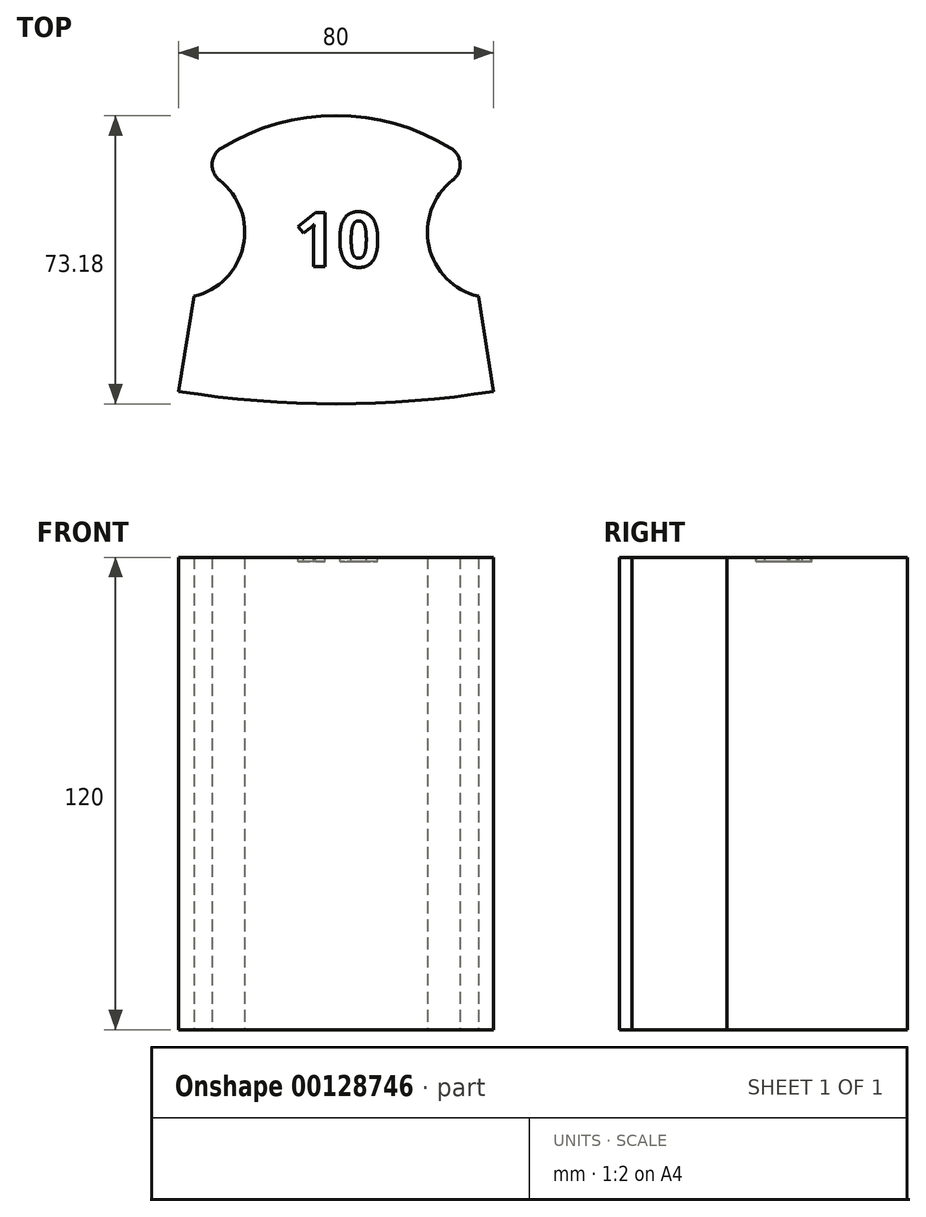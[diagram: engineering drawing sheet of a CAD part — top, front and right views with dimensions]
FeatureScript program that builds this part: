
annotation { "Feature Type Name" : "Feature", "Feature Type Description" : "" }
export const myFeature = defineFeature(function(context is Context, id is Id, definition is map)
    precondition{}
    {
        {
            var Q0;
            Q0=qCreatedBy(makeId("Top.planeOp"),FACE);
            var sketch = newSketch(context, id + "F0", { "sketchPlane" : qUnion([Q0])});
            skLineSegment(sketch, "E0", {"start": v(0, 0) * mm, "end": v(3.87, 24.16) * mm});
            skLineSegment(sketch, "E1", {"start": v(0, 0) * mm, "end": v(80, 0) * mm, "construction": true});
            skLineSegment(sketch, "E2", {"start": v(40, 0) * mm, "end": v(40, 70) * mm, "construction": true});
            skArc(sketch, "E3", {"start": v(3.87, 24.16) * mm, "mid": v(16.4, 36.85) * mm, "end": v(10.4, 53.64) * mm});
            skArc(sketch, "E4.MirrorCS", {"start": v(76.13, 24.16) * mm, "mid": v(63.6, 36.85) * mm, "end": v(69.6, 53.64) * mm});
            skLineSegment(sketch, "E5.MirrorCS", {"start": v(80, 0) * mm, "end": v(76.13, 24.16) * mm});
            skArc(sketch, "E6", {"start": v(69.1, 61.84) * mm, "mid": v(40, 70) * mm, "end": v(10.9, 61.84) * mm});
            skPoint(sketch, "E7.visualSharp", {"position": v(3.87, 56.79) * mm});
            skArc(sketch, "E7.filletArc", {"start": v(10.9, 61.84) * mm, "mid": v(8.5, 57.87) * mm, "end": v(10.4, 53.64) * mm});
            skPoint(sketch, "E8.visualSharp", {"position": v(76.13, 56.79) * mm});
            skArc(sketch, "E8.filletArc", {"start": v(69.6, 53.64) * mm, "mid": v(71.5, 57.87) * mm, "end": v(69.1, 61.84) * mm});
            skArc(sketch, "E9", {"start": v(0, 0) * mm, "mid": v(40, -3.18) * mm, "end": v(80, 0) * mm});
            skSolve(sketch);
        }
        {
            var Q0;
            Q0=makeQuery(id+"F0.imprint","IMPRINT",FACE,{"disambiguationData":[TD([[makeQuery(id+"F0.imprint","IMPRINT",EDGE,{"derivedFrom":sQuery(id+"F0.wireOp",EDGE,"E0")}),-1.0]])]});
            extrude(context, id + "F1", {"entities" : qUnion([Q0]), "depth" : 120 * mm});
        }
        {
            var Q0;
            Q0=makeQuery(id+"F1.opExtrude","CAP_FACE",FACE,{"disambiguationData":[OSD([sQuery(id+"F0.wireOp",EDGE,"E0"),sQuery(id+"F0.wireOp",EDGE,"E3"),sQuery(id+"F0.wireOp",EDGE,"E4.MirrorCS"),sQuery(id+"F0.wireOp",EDGE,"E5.MirrorCS"),sQuery(id+"F0.wireOp",EDGE,"E6"),sQuery(id+"F0.wireOp",EDGE,"E7.filletArc"),sQuery(id+"F0.wireOp",EDGE,"E8.filletArc"),sQuery(id+"F0.wireOp",EDGE,"E9")])],"isStart":false});
            var sketch = newSketch(context, id + "F2", { "sketchPlane" : qUnion([Q0])});
            skText(sketch, "E10", { "text": "10", "fontName": "OpenSans-Bold.ttf"});
            skPoint(sketch, "E11", {"position": v(40, 70) * mm});
            const initialGuessF2  = {"E10": [0.02922, 0.03166, 1, 0, 0.0139]};
            skSetInitialGuess(sketch, initialGuessF2);
            skSolve(sketch);
        }
        {
            var Q0;
            Q0 = qSketchRegion(id + "F2", true);
            extrude(context, id + "F3", {"entities" : qUnion([Q0]), "operationType" : NewBodyOperationType.REMOVE, "oppositeDirection" : true, "depth" : 1 * mm});
        }
    });
